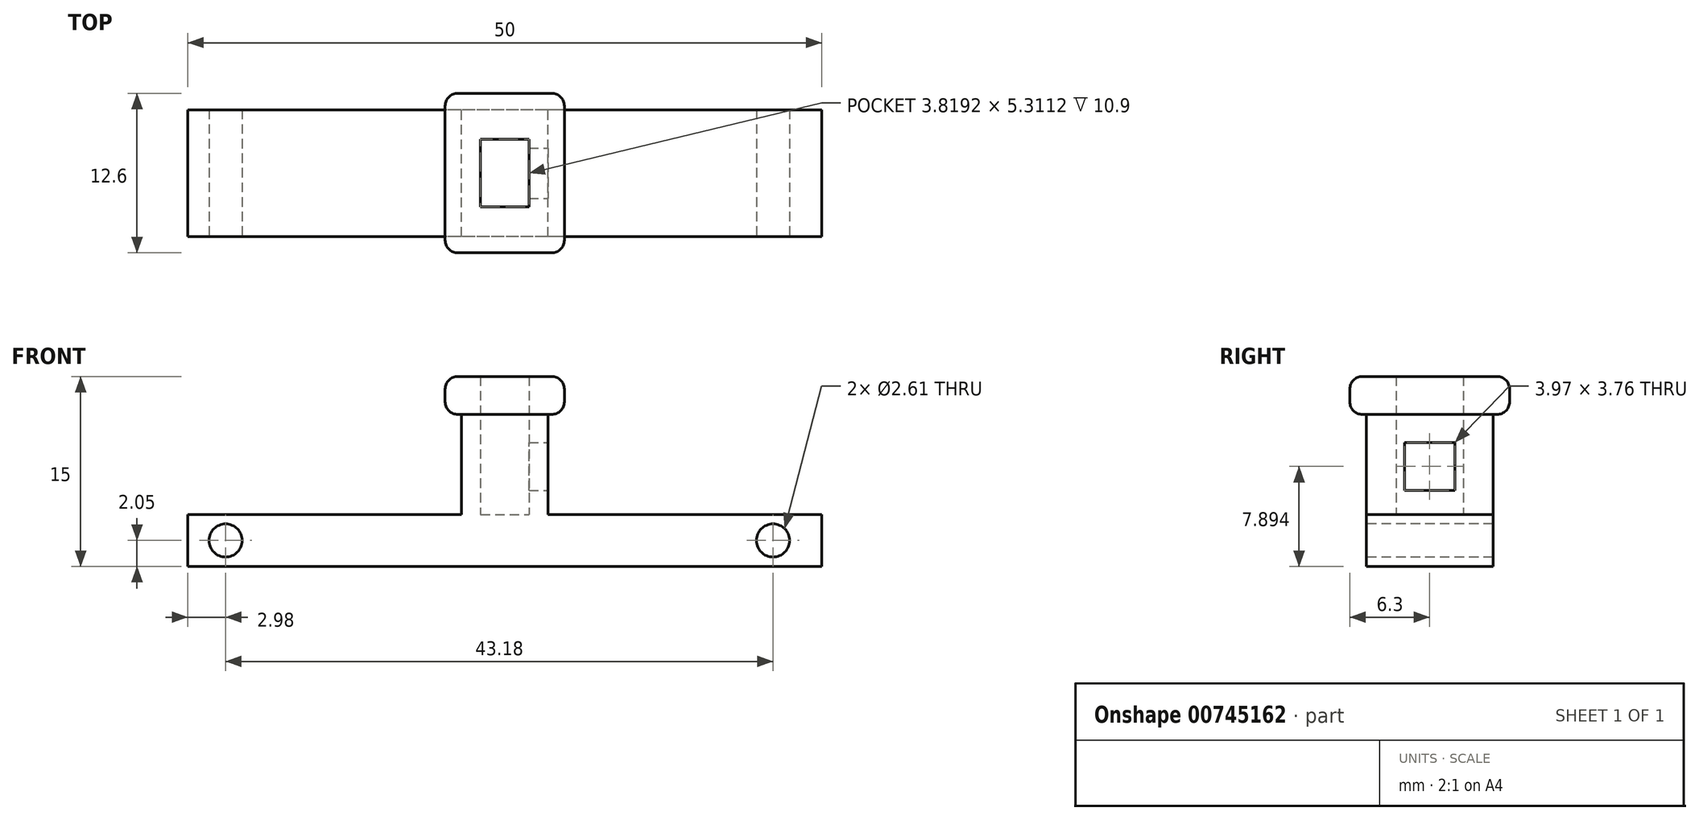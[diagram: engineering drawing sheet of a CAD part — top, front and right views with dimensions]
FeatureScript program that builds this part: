
annotation { "Feature Type Name" : "Feature", "Feature Type Description" : "" }
export const myFeature = defineFeature(function(context is Context, id is Id, definition is map)
    precondition{}
    {
        {
            var Q0;
            Q0=qCreatedBy(makeId("Top.planeOp"),FACE);
            var sketch = newSketch(context, id + "F0", { "sketchPlane" : qUnion([Q0])});
            skLineSegment(sketch, "E0.bottom", {"start": v(25, -5) * mm, "end": v(-25, -5) * mm});
            skLineSegment(sketch, "E0.top", {"start": v(25, 5) * mm, "end": v(-25, 5) * mm});
            skLineSegment(sketch, "E0.left", {"start": v(25, -5) * mm, "end": v(25, 5) * mm});
            skLineSegment(sketch, "E0.right", {"start": v(-25, -5) * mm, "end": v(-25, 5) * mm});
            skPoint(sketch, "E0.middle", {"position": v(0, 0) * mm});
            skLineSegment(sketch, "E1.bottom", {"start": v(3.4, -5) * mm, "end": v(-3.4, -5) * mm});
            skLineSegment(sketch, "E1.top", {"start": v(3.4, 5) * mm, "end": v(-3.4, 5) * mm});
            skLineSegment(sketch, "E1.left", {"start": v(3.4, -5) * mm, "end": v(3.4, 5) * mm});
            skLineSegment(sketch, "E1.right", {"start": v(-3.4, -5) * mm, "end": v(-3.4, 5) * mm});
            skLineSegment(sketch, "E2.bottom", {"start": v(1.9, -2.66) * mm, "end": v(-1.9, -2.66) * mm});
            skLineSegment(sketch, "E2.top", {"start": v(1.9, 2.66) * mm, "end": v(-1.9, 2.66) * mm});
            skLineSegment(sketch, "E2.left", {"start": v(1.9, -2.66) * mm, "end": v(1.9, 2.66) * mm});
            skLineSegment(sketch, "E2.right", {"start": v(-1.9, -2.66) * mm, "end": v(-1.9, 2.66) * mm});
            skSolve(sketch);
        }
        {
            var Q0;
            {var subQ2=sQuery(id+"F0.wireOp",EDGE,"E0.right");Q0=makeQuery(id+"F0.imprint","IMPRINT",FACE,{"disambiguationData":[TD([[makeQuery(id+"F0.imprint","IMPRINT",EDGE,{"derivedFrom":subQ2}),-1.0]])]});}
            var Q1;
            {var subQ0=sQuery(id+"F0.wireOp",EDGE,"E0.left");Q1=makeQuery(id+"F0.imprint","IMPRINT",FACE,{"disambiguationData":[TD([[makeQuery(id+"F0.imprint","IMPRINT",EDGE,{"derivedFrom":subQ0}),1.0]])]});}
            var Q2;
            {var subQ1=sQuery(id+"F0.wireOp",EDGE,"E1.left");Q2=makeQuery(id+"F0.imprint","IMPRINT",FACE,{"disambiguationData":[TD([[makeQuery(id+"F0.imprint","IMPRINT",EDGE,{"derivedFrom":subQ1}),1.0]])]});}
            var Q3;
            Q3=makeQuery(id+"F0.imprint","IMPRINT",FACE,{"disambiguationData":[TD([[makeQuery(id+"F0.imprint","IMPRINT",EDGE,{"derivedFrom":sQuery(id+"F0.wireOp",EDGE,"E2.bottom")}),-1.0]])]});
            extrude(context, id + "F1", {"entities" : qUnion([Q0, Q1, Q2, Q3]), "depth" : 4.1 * mm, "offsetDistance" : 25 * mm});
        }
        {
            var Q0;
            {var subQ1=sQuery(id+"F0.wireOp",EDGE,"E1.left");Q0=makeQuery(id+"F0.imprint","IMPRINT",FACE,{"disambiguationData":[TD([[makeQuery(id+"F0.imprint","IMPRINT",EDGE,{"derivedFrom":subQ1}),1.0]])]});}
            extrude(context, id + "F2", {"entities" : qUnion([Q0]), "operationType" : NewBodyOperationType.ADD, "depth" : 15 * mm, "offsetDistance" : 25 * mm});
        }
        {
            var Q0;
            Q0=makeQuery(id+"F2.opExtrude","SWEPT_FACE",FACE,{"disambiguationData":[OSD([sQuery(id+"F0.wireOp",EDGE,"E1.left")])]});
            var sketch = newSketch(context, id + "F3", { "sketchPlane" : qUnion([Q0])});
            skLineSegment(sketch, "E3.bottom", {"start": v(1.99, 6.02) * mm, "end": v(-1.99, 6.02) * mm});
            skLineSegment(sketch, "E3.top", {"start": v(1.99, 9.77) * mm, "end": v(-1.99, 9.77) * mm});
            skLineSegment(sketch, "E3.left", {"start": v(1.99, 6.02) * mm, "end": v(1.99, 9.77) * mm});
            skLineSegment(sketch, "E3.right", {"start": v(-1.99, 6.02) * mm, "end": v(-1.99, 9.77) * mm});
            skPoint(sketch, "E3.middle", {"position": v(0, 7.9) * mm});
            skSolve(sketch);
        }
        {
            var Q0;
            Q0=makeQuery(id+"F3.imprint","IMPRINT",FACE,{"disambiguationData":[TD([[makeQuery(id+"F3.imprint","IMPRINT",EDGE,{"derivedFrom":sQuery(id+"F3.wireOp",EDGE,"E3.bottom")}),-1.0]])]});
            extrude(context, id + "F4", {"entities" : qUnion([Q0]), "operationType" : NewBodyOperationType.REMOVE, "endBound" : BoundingType.UP_TO_NEXT, "oppositeDirection" : true, "depth" : 25 * mm, "offsetDistance" : 25 * mm});
        }
        {
            var Q0;
            {var subQ0=sQuery(id+"F0.wireOp",EDGE,"E0.bottom");Q0=makeQuery(id+"F2.boolean.opBoolean","MERGE",FACE,{"derivedFrom":[makeQuery(id+"F1.opExtrude","SWEPT_FACE",FACE,{"disambiguationData":[OSD([subQ0])]}),makeQuery(id+"F2.opExtrude","SWEPT_FACE",FACE,{"disambiguationData":[OSD([subQ0])]})]});}
            var sketch = newSketch(context, id + "F5", { "sketchPlane" : qUnion([Q0])});
            skCircle(sketch, "E4", {"center": v(-22.02, 2.05) * mm, "radius": 1.3 * mm});
            skPoint(sketch, "E4.centerSnap0", {"position": v(-25, 2.05) * mm});
            skCircle(sketch, "E5", {"center": v(21.16, 2.05) * mm, "radius": 1.3 * mm});
            skPoint(sketch, "E5.centerSnap0", {"position": v(25, 2.05) * mm});
            skSolve(sketch);
        }
        {
            var Q0;
            Q0=makeQuery(id+"F5.imprint","IMPRINT",FACE,{"disambiguationData":[TD([[makeQuery(id+"F5.imprint","IMPRINT",EDGE,{"derivedFrom":sQuery(id+"F5.wireOp",EDGE,"E4")}),1.0]])]});
            var Q1;
            Q1=makeQuery(id+"F5.imprint","IMPRINT",FACE,{"disambiguationData":[TD([[makeQuery(id+"F5.imprint","IMPRINT",EDGE,{"derivedFrom":sQuery(id+"F5.wireOp",EDGE,"E5")}),1.0]])]});
            extrude(context, id + "F6", {"entities" : qUnion([Q0, Q1]), "operationType" : NewBodyOperationType.REMOVE, "endBound" : BoundingType.THROUGH_ALL, "oppositeDirection" : true, "depth" : 25 * mm, "offsetDistance" : 25 * mm});
        }
        {
            var Q0;
            Q0=makeQuery(id+"F2.opExtrude","CAP_FACE",FACE,{"disambiguationData":[OSD([sQuery(id+"F0.wireOp",EDGE,"E0.bottom"),sQuery(id+"F0.wireOp",EDGE,"E0.top"),sQuery(id+"F0.wireOp",EDGE,"E1.left"),sQuery(id+"F0.wireOp",EDGE,"E1.right"),sQuery(id+"F0.wireOp",EDGE,"E2.bottom"),sQuery(id+"F0.wireOp",EDGE,"E2.top"),sQuery(id+"F0.wireOp",EDGE,"E2.left"),sQuery(id+"F0.wireOp",EDGE,"E2.right")])],"isStart":false});
            var sketch = newSketch(context, id + "F7", { "sketchPlane" : qUnion([Q0])});
            skLineSegment(sketch, "E6.0", {"start": v(4.7, -6.3) * mm, "end": v(4.7, 6.3) * mm});
            skLineSegment(sketch, "E6.1", {"start": v(4.7, -6.3) * mm, "end": v(-4.7, -6.3) * mm});
            skLineSegment(sketch, "E6.2", {"start": v(-4.7, -6.3) * mm, "end": v(-4.7, 6.3) * mm});
            skLineSegment(sketch, "E6.3", {"start": v(4.7, 6.3) * mm, "end": v(-4.7, 6.3) * mm});
            skSolve(sketch);
        }
        {
            var Q0;
            Q0=makeQuery(id+"F7.imprint","IMPRINT",FACE,{"disambiguationData":[TD([[makeQuery(id+"F7.imprint","IMPRINT",EDGE,{"derivedFrom":makeQuery(id+"F2.opExtrude","CAP_EDGE",EDGE,{"disambiguationData":[OSD([sQuery(id+"F0.wireOp",EDGE,"E0.bottom")])],"isStart":false})}),-1.0]])]});
            var Q1;
            Q1=makeQuery(id+"F7.imprint","IMPRINT",FACE,{"disambiguationData":[TD([[makeQuery(id+"F7.imprint","IMPRINT",EDGE,{"derivedFrom":sQuery(id+"F7.wireOp",EDGE,"E6.0")}),1.0]])]});
            extrude(context, id + "F8", {"entities" : qUnion([Q0, Q1]), "operationType" : NewBodyOperationType.ADD, "oppositeDirection" : true, "depth" : 3 * mm, "offsetDistance" : 25 * mm});
        }
        {
            var Q0;
            Q0=makeQuery(id+"F8.opExtrude","CAP_EDGE",EDGE,{"disambiguationData":[OSD([sQuery(id+"F7.wireOp",EDGE,"E6.2")])],"isStart":true});
            var Q1;
            Q1=makeQuery(id+"F8.opExtrude","CAP_EDGE",EDGE,{"disambiguationData":[OSD([sQuery(id+"F7.wireOp",EDGE,"E6.1")])],"isStart":true});
            var Q2;
            Q2=makeQuery(id+"F8.opExtrude","CAP_EDGE",EDGE,{"disambiguationData":[OSD([sQuery(id+"F7.wireOp",EDGE,"E6.1")])],"isStart":false});
            var Q3;
            Q3=makeQuery(id+"F8.opExtrude","CAP_EDGE",EDGE,{"disambiguationData":[OSD([sQuery(id+"F7.wireOp",EDGE,"E6.0")])],"isStart":false});
            var Q4;
            Q4=makeQuery(id+"F8.opExtrude","CAP_EDGE",EDGE,{"disambiguationData":[OSD([sQuery(id+"F7.wireOp",EDGE,"E6.3")])],"isStart":true});
            var Q5;
            Q5=makeQuery(id+"F8.opExtrude","CAP_EDGE",EDGE,{"disambiguationData":[OSD([sQuery(id+"F7.wireOp",EDGE,"E6.2")])],"isStart":false});
            var Q6;
            Q6=makeQuery(id+"F8.opExtrude","CAP_EDGE",EDGE,{"disambiguationData":[OSD([sQuery(id+"F7.wireOp",EDGE,"E6.3")])],"isStart":false});
            var Q7;
            Q7=makeQuery(id+"F8.opExtrude","CAP_EDGE",EDGE,{"disambiguationData":[OSD([sQuery(id+"F7.wireOp",EDGE,"E6.0")])],"isStart":true});
            var Q8;
            Q8=makeQuery(id+"F8.opExtrude","SWEPT_EDGE",EDGE,{"disambiguationData":[OSD([sQuery(id+"F7.wireOp",EDGE,"E6.0"),sQuery(id+"F7.wireOp",EDGE,"E6.1")])]});
            var Q9;
            Q9=makeQuery(id+"F8.opExtrude","SWEPT_EDGE",EDGE,{"disambiguationData":[OSD([sQuery(id+"F7.wireOp",EDGE,"E6.0"),sQuery(id+"F7.wireOp",EDGE,"E6.3")])]});
            var Q10;
            Q10=makeQuery(id+"F8.opExtrude","SWEPT_EDGE",EDGE,{"disambiguationData":[OSD([sQuery(id+"F7.wireOp",EDGE,"E6.2"),sQuery(id+"F7.wireOp",EDGE,"E6.3")])]});
            var Q11;
            Q11=makeQuery(id+"F8.opExtrude","SWEPT_EDGE",EDGE,{"disambiguationData":[OSD([sQuery(id+"F7.wireOp",EDGE,"E6.1"),sQuery(id+"F7.wireOp",EDGE,"E6.2")])]});
            fillet(context, id + "F9", {"entities" : qUnion([Q0, Q1, Q2, Q3, Q4, Q5, Q6, Q7, Q8, Q9, Q10, Q11]), "radius" : 1 * mm, "tangentPropagation" : true, "allowEdgeOverflow" : false});
        }
    });
